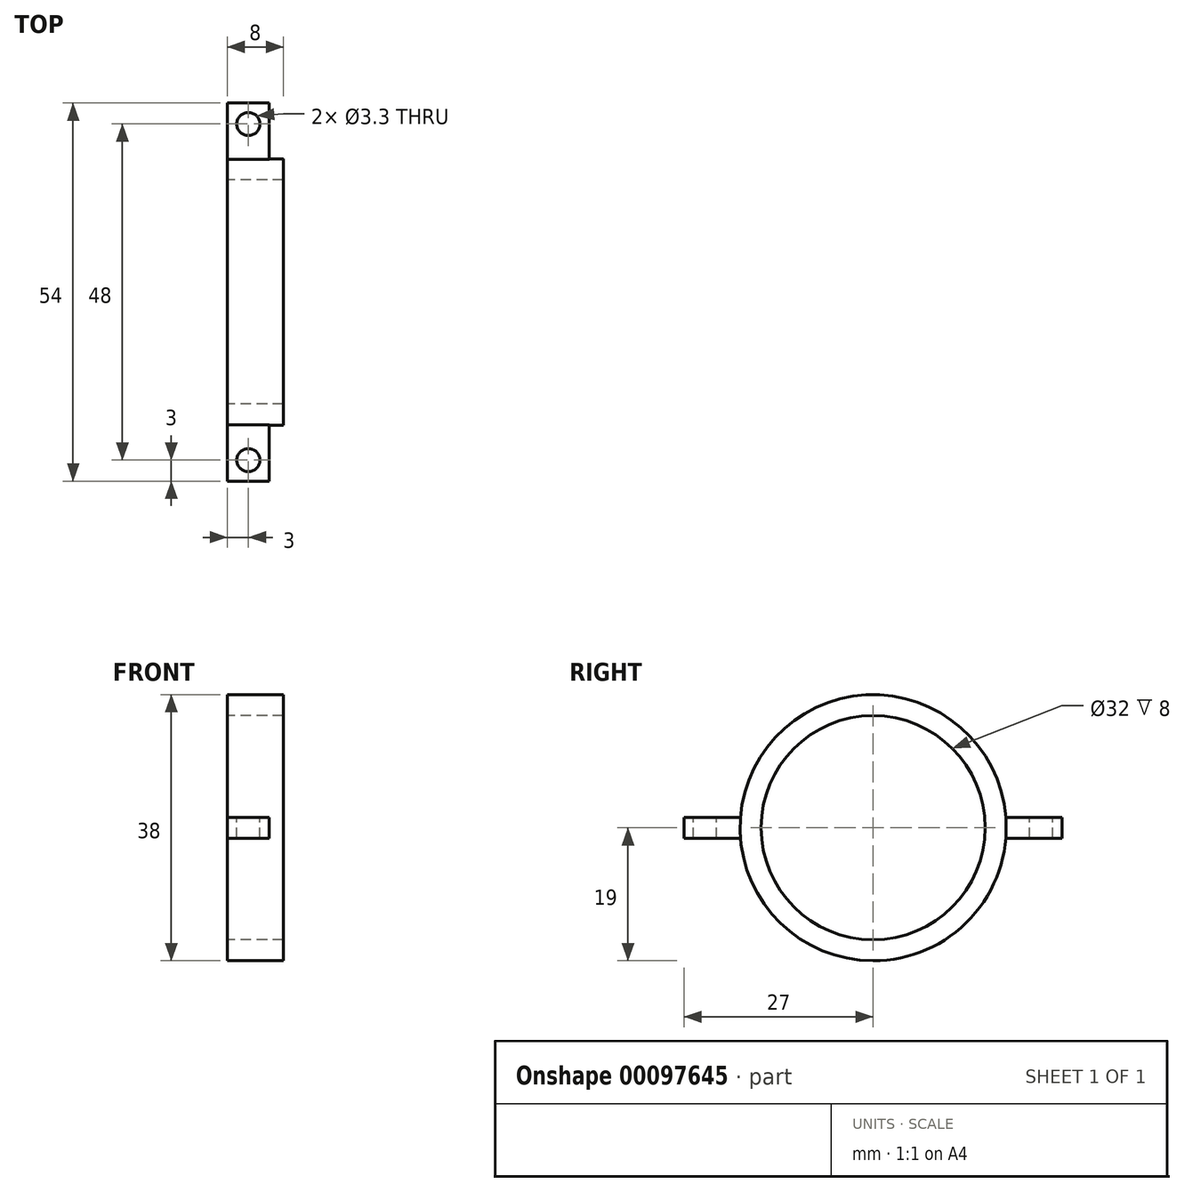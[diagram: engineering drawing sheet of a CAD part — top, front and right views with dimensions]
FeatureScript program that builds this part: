
annotation { "Feature Type Name" : "Feature", "Feature Type Description" : "" }
export const myFeature = defineFeature(function(context is Context, id is Id, definition is map)
    precondition{}
    {
        {
            var Q0;
            Q0=qCreatedBy(makeId("Right.planeOp"),FACE);
            var sketch = newSketch(context, id + "F0", { "sketchPlane" : qUnion([Q0])});
            skCircle(sketch, "E0", {"center": v(0, 0) * mm, "radius": 19 * mm});
            skCircle(sketch, "E1", {"center": v(0, 0) * mm, "radius": 16 * mm});
            skSolve(sketch);
        }
        {
            var Q0;
            Q0=makeQuery(id+"F0.imprint","IMPRINT",FACE,{"disambiguationData":[TD([[makeQuery(id+"F0.imprint","IMPRINT",EDGE,{"derivedFrom":sQuery(id+"F0.wireOp",EDGE,"E0")}),1.0]])]});
            extrude(context, id + "F1", {"entities" : qUnion([Q0]), "endBound" : BoundingType.SYMMETRIC, "depth" : 8 * mm});
        }
        {
            var Q0;
            Q0=qCreatedBy(makeId("Front.planeOp"),FACE);
            var sketch = newSketch(context, id + "F2", { "sketchPlane" : qUnion([Q0])});
            skLineSegment(sketch, "E2.bottom", {"start": v(2, -1.5) * mm, "end": v(-4, -1.5) * mm});
            skLineSegment(sketch, "E2.top", {"start": v(2, 1.5) * mm, "end": v(-4, 1.5) * mm});
            skLineSegment(sketch, "E2.left", {"start": v(2, -1.5) * mm, "end": v(2, 1.5) * mm});
            skLineSegment(sketch, "E2.right", {"start": v(-4, -1.5) * mm, "end": v(-4, 1.5) * mm});
            skPoint(sketch, "E2.middle", {"position": v(0, 0) * mm});
            skSolve(sketch);
        }
        {
            var Q0;
            Q0=makeQuery(id+"F2.imprint","IMPRINT",FACE,{"disambiguationData":[TD([[makeQuery(id+"F2.imprint","IMPRINT",EDGE,{"derivedFrom":sQuery(id+"F2.wireOp",EDGE,"E2.bottom")}),-1.0]])]});
            var Q1;
            Q1=makeQuery(id+"F1.opExtrude","SWEPT_FACE",FACE,{"disambiguationData":[OSD([sQuery(id+"F0.wireOp",EDGE,"E0")])]});
            extrude(context, id + "F3", {"entities" : qUnion([Q0]), "operationType" : NewBodyOperationType.ADD, "endBound" : BoundingType.SYMMETRIC, "depth" : 54 * mm});
        }
        {
            var Q0;
            {var subQ2=sQuery(id+"F2.wireOp",EDGE,"E2.right");var subQ3=sQuery(id+"F2.wireOp",EDGE,"E2.left");var subQ4=sQuery(id+"F2.wireOp",EDGE,"E2.top");Q0=makeQuery(id+"F3.boolean.opBoolean","SPLIT",FACE,{"disambiguationData":[TD([makeQuery(id+"F3.opExtrude","CAP_FACE",FACE,{"disambiguationData":[OSD([sQuery(id+"F2.wireOp",EDGE,"E2.bottom"),subQ4,subQ3,subQ2])],"isStart":true})])],"derivedFrom":makeQuery(id+"F3.opExtrude","SWEPT_FACE",FACE,{"disambiguationData":[OSD([subQ4])]})});}
            var sketch = newSketch(context, id + "F4", { "sketchPlane" : qUnion([Q0])});
            skPoint(sketch, "E3", {"position": v(-1, 24) * mm});
            skPoint(sketch, "E4.MirrorP", {"position": v(-1, -24) * mm});
            skSolve(sketch);
        }
        {
            var Q0;
            Q0=makeQuery(id+"F0.imprint","IMPRINT",FACE,{"disambiguationData":[TD([[makeQuery(id+"F0.imprint","IMPRINT",EDGE,{"derivedFrom":sQuery(id+"F0.wireOp",EDGE,"E1")}),1.0]])]});
            extrude(context, id + "F5", {"entities" : qUnion([Q0]), "operationType" : NewBodyOperationType.REMOVE, "endBound" : BoundingType.SYMMETRIC, "depth" : 8 * mm});
        }
        {
            var Q0;
            Q0=sQuery(id+"F4.wireOp",VERTEX,"E3");
            var Q1;
            Q1=sQuery(id+"F4.wireOp",VERTEX,"E4.MirrorP");
            var Q2;
            Q2=makeQuery(id+"F1.opExtrude","SWEPT_BODY",BODY,{"disambiguationData":[OSD([sQuery(id+"F0.wireOp",EDGE,"E0"),sQuery(id+"F0.wireOp",EDGE,"E1")])]});
            hole(context, id + "F6", {"style" : HoleStyle.SIMPLE, "endStyle" : HoleEndStyle.BLIND, "standardTappedOrClearance" : lookupTablePath({ "standard" : "ISO", "fit" : "Normal", "size" : "M3", "type" : "Clearance" }), "standardBlindInLast" : lookupTablePath({ "fit" : "Standard", "standard" : "ISO", "size" : "M3", "type" : "Clearance" }), "holeDiameter" : 3.3 * mm, "holeDepth" : 7 * mm, "locations" : qUnion([Q0, Q1]), "scope" : qUnion([Q2])});
        }
    });
